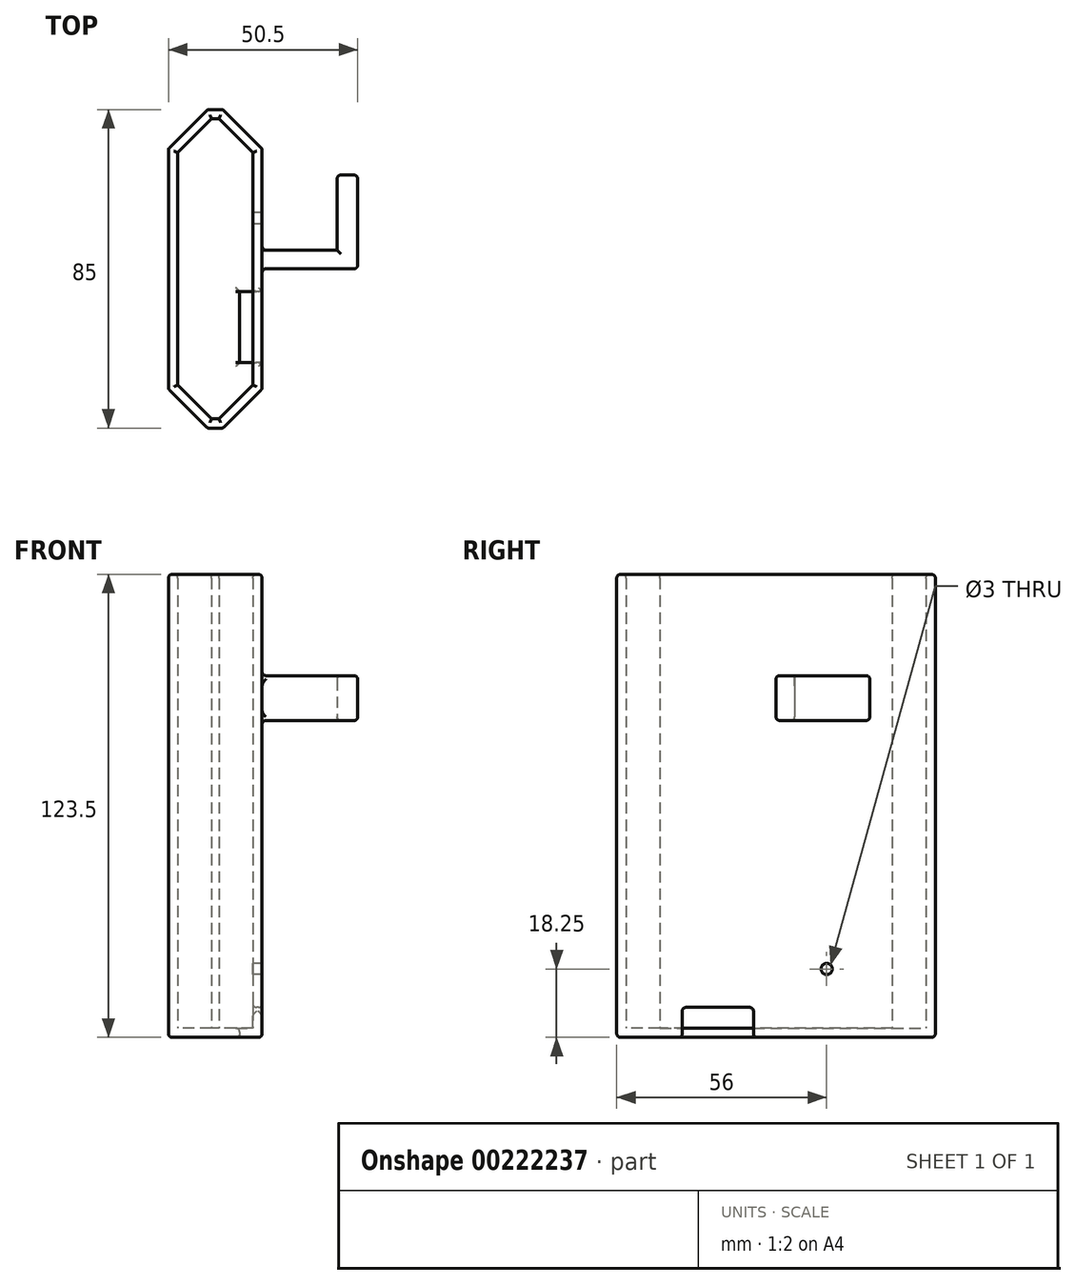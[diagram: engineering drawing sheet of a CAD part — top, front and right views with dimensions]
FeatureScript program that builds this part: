
annotation { "Feature Type Name" : "Feature", "Feature Type Description" : "" }
export const myFeature = defineFeature(function(context is Context, id is Id, definition is map)
    precondition{}
    {
        {
            var Q0;
            Q0=qCreatedBy(makeId("Top.planeOp"),FACE);
            var sketch = newSketch(context, id + "F0", { "sketchPlane" : qUnion([Q0])});
            skPoint(sketch, "E0.middle", {"position": v(0, 0) * mm});
            skPoint(sketch, "E1", {"position": v(-10, 31) * mm});
            skPoint(sketch, "E2", {"position": v(10, 31) * mm});
            skPoint(sketch, "E3", {"position": v(10, -31) * mm});
            skPoint(sketch, "E4", {"position": v(-10, -31) * mm});
            skPoint(sketch, "E5", {"position": v(-1, 40) * mm});
            skPoint(sketch, "E6", {"position": v(-1, -40) * mm});
            skPoint(sketch, "E7", {"position": v(1, 40) * mm});
            skPoint(sketch, "E8", {"position": v(1, -40) * mm});
            skLineSegment(sketch, "E9", {"start": v(1, 40) * mm, "end": v(-1, 40) * mm});
            skLineSegment(sketch, "E10", {"start": v(-1, 40) * mm, "end": v(-10, 31) * mm});
            skLineSegment(sketch, "E11", {"start": v(-10, 31) * mm, "end": v(-10, -31) * mm});
            skLineSegment(sketch, "E12", {"start": v(-10, -31) * mm, "end": v(-1, -40) * mm});
            skLineSegment(sketch, "E13", {"start": v(-1, -40) * mm, "end": v(1, -40) * mm});
            skLineSegment(sketch, "E14", {"start": v(1, -40) * mm, "end": v(10, -31) * mm});
            skLineSegment(sketch, "E15", {"start": v(10, -31) * mm, "end": v(10, 31) * mm});
            skLineSegment(sketch, "E16", {"start": v(10, 31) * mm, "end": v(1, 40) * mm});
            skLineSegment(sketch, "E17.0", {"start": v(12.5, 32.04) * mm, "end": v(2.04, 42.5) * mm});
            skLineSegment(sketch, "E17.1", {"start": v(12.5, -32.04) * mm, "end": v(12.5, 32.04) * mm});
            skLineSegment(sketch, "E17.2", {"start": v(2.04, 42.5) * mm, "end": v(-2.04, 42.5) * mm});
            skLineSegment(sketch, "E17.3", {"start": v(2.04, -42.5) * mm, "end": v(12.5, -32.04) * mm});
            skLineSegment(sketch, "E17.4", {"start": v(-2.04, 42.5) * mm, "end": v(-12.5, 32.04) * mm});
            skLineSegment(sketch, "E17.5", {"start": v(-12.5, 32.04) * mm, "end": v(-12.5, -32.04) * mm});
            skLineSegment(sketch, "E17.6", {"start": v(-12.5, -32.04) * mm, "end": v(-2.04, -42.5) * mm});
            skLineSegment(sketch, "E17.7", {"start": v(-2.04, -42.5) * mm, "end": v(2.04, -42.5) * mm});
            skSolve(sketch);
        }
        {
            var Q0;
            Q0=makeQuery(id+"F0.imprint","IMPRINT",FACE,{"disambiguationData":[TD([[makeQuery(id+"F0.imprint","IMPRINT",EDGE,{"derivedFrom":sQuery(id+"F0.wireOp",EDGE,"E9")}),1.0]])]});
            extrude(context, id + "F1", {"entities" : qUnion([Q0]), "depth" : 2.5 * mm, "offsetDistance" : 25 * mm});
        }
        {
            var Q0;
            Q0=makeQuery(id+"F0.imprint","IMPRINT",FACE,{"disambiguationData":[TD([[makeQuery(id+"F0.imprint","IMPRINT",EDGE,{"derivedFrom":sQuery(id+"F0.wireOp",EDGE,"E9")}),-1.0]])]});
            extrude(context, id + "F2", {"entities" : qUnion([Q0]), "operationType" : NewBodyOperationType.ADD, "depth" : 123.5 * mm, "offsetDistance" : 25 * mm});
        }
        {
            var Q0;
            {var subQ0=sQuery(id+"F0.wireOp",EDGE,"E16");var subQ1=sQuery(id+"F0.wireOp",EDGE,"E15");var subQ2=sQuery(id+"F0.wireOp",EDGE,"E14");var subQ3=sQuery(id+"F0.wireOp",EDGE,"E13");var subQ4=sQuery(id+"F0.wireOp",EDGE,"E12");var subQ5=sQuery(id+"F0.wireOp",EDGE,"E11");var subQ6=sQuery(id+"F0.wireOp",EDGE,"E10");var subQ7=sQuery(id+"F0.wireOp",EDGE,"E9");Q0=makeQuery(id+"F2.boolean.opBoolean","MERGE",FACE,{"derivedFrom":[makeQuery(id+"F1.opExtrude","CAP_FACE",FACE,{"disambiguationData":[OSD([subQ7,subQ6,subQ5,subQ4,subQ3,subQ2,subQ1,subQ0])],"isStart":true}),makeQuery(id+"F2.opExtrude","CAP_FACE",FACE,{"disambiguationData":[OSD([subQ7,subQ6,subQ5,subQ4,subQ3,subQ2,subQ1,subQ0,sQuery(id+"F0.wireOp",EDGE,"E17.0"),sQuery(id+"F0.wireOp",EDGE,"E17.1"),sQuery(id+"F0.wireOp",EDGE,"E17.2"),sQuery(id+"F0.wireOp",EDGE,"E17.3"),sQuery(id+"F0.wireOp",EDGE,"E17.4"),sQuery(id+"F0.wireOp",EDGE,"E17.5"),sQuery(id+"F0.wireOp",EDGE,"E17.6"),sQuery(id+"F0.wireOp",EDGE,"E17.7")])],"isStart":true})]});}
            var sketch = newSketch(context, id + "F3", { "sketchPlane" : qUnion([Q0])});
            skPoint(sketch, "E18", {"position": v(12.5, 25.04) * mm});
            skPoint(sketch, "E19", {"position": v(12.5, 32.04) * mm});
            skLineSegment(sketch, "E20.bottom", {"start": v(12.5, 25.04) * mm, "end": v(6.5, 25.04) * mm});
            skLineSegment(sketch, "E20.top", {"start": v(12.5, 6.04) * mm, "end": v(6.5, 6.04) * mm});
            skLineSegment(sketch, "E20.left", {"start": v(12.5, 25.04) * mm, "end": v(12.5, 6.04) * mm});
            skLineSegment(sketch, "E20.right", {"start": v(6.5, 25.04) * mm, "end": v(6.5, 6.04) * mm});
            skPoint(sketch, "E21", {"position": v(12.5, 0) * mm});
            skPoint(sketch, "E22", {"position": v(-12.5, 0) * mm});
            skSolve(sketch);
        }
        {
            var Q0;
            Q0=makeQuery(id+"F3.imprint","IMPRINT",FACE,{"disambiguationData":[TD([[makeQuery(id+"F3.imprint","IMPRINT",EDGE,{"derivedFrom":sQuery(id+"F3.wireOp",EDGE,"E20.bottom")}),1.0]])]});
            extrude(context, id + "F4", {"entities" : qUnion([Q0]), "operationType" : NewBodyOperationType.REMOVE, "oppositeDirection" : true, "depth" : 8 * mm, "offsetDistance" : 25 * mm});
        }
        {
            var Q0;
            Q0=makeQuery(id+"F2.opExtrude","SWEPT_FACE",FACE,{"disambiguationData":[OSD([sQuery(id+"F0.wireOp",EDGE,"E17.1")])]});
            var sketch = newSketch(context, id + "F5", { "sketchPlane" : qUnion([Q0])});
            skPoint(sketch, "E23", {"position": v(0, 18.25) * mm});
            skPoint(sketch, "E24", {"position": v(13.5, 18.25) * mm});
            skPoint(sketch, "E25", {"position": v(0, 96.5) * mm});
            skPoint(sketch, "E26", {"position": v(0, 84.5) * mm});
            skLineSegment(sketch, "E27.bottom", {"start": v(0, 96.5) * mm, "end": v(5, 96.5) * mm});
            skLineSegment(sketch, "E27.top", {"start": v(0, 84.5) * mm, "end": v(5, 84.5) * mm});
            skLineSegment(sketch, "E27.left", {"start": v(0, 96.5) * mm, "end": v(0, 84.5) * mm});
            skLineSegment(sketch, "E27.right", {"start": v(5, 96.5) * mm, "end": v(5, 84.5) * mm});
            skLineSegment(sketch, "E28.bottom", {"start": v(5, 96.5) * mm, "end": v(25, 96.5) * mm});
            skLineSegment(sketch, "E28.top", {"start": v(5, 84.5) * mm, "end": v(25, 84.5) * mm});
            skLineSegment(sketch, "E28.right", {"start": v(25, 96.5) * mm, "end": v(25, 84.5) * mm});
            skSolve(sketch);
        }
        {
            var Q0;
            Q0=sQuery(id+"F5.wireOp",VERTEX,"E24");
            var Q1;
            Q1=makeQuery(id+"F1.opExtrude","SWEPT_BODY",BODY,{"disambiguationData":[OSD([sQuery(id+"F0.wireOp",EDGE,"E9"),sQuery(id+"F0.wireOp",EDGE,"E10"),sQuery(id+"F0.wireOp",EDGE,"E11"),sQuery(id+"F0.wireOp",EDGE,"E12"),sQuery(id+"F0.wireOp",EDGE,"E13"),sQuery(id+"F0.wireOp",EDGE,"E14"),sQuery(id+"F0.wireOp",EDGE,"E15"),sQuery(id+"F0.wireOp",EDGE,"E16")])]});
            hole(context, id + "F6", {"style" : HoleStyle.SIMPLE, "endStyle" : HoleEndStyle.BLIND, "holeDiameter" : 3 * mm, "majorDiameter" : 5 * mm, "holeDepth" : 5 * mm, "isTappedThrough" : true, "tappedDepth" : 12 * mm, "tapClearance" : 3, "locations" : qUnion([Q0]), "scope" : qUnion([Q1])});
        }
        {
            var Q0;
            Q0=makeQuery(id+"F5.imprint","IMPRINT",FACE,{"disambiguationData":[TD([[makeQuery(id+"F5.imprint","IMPRINT",EDGE,{"derivedFrom":sQuery(id+"F5.wireOp",EDGE,"E27.bottom")}),-1.0]])]});
            extrude(context, id + "F7", {"entities" : qUnion([Q0]), "operationType" : NewBodyOperationType.ADD, "depth" : 25.5 * mm, "offsetDistance" : 25 * mm});
        }
        {
            var Q0;
            Q0=makeQuery(id+"F5.imprint","IMPRINT",FACE,{"disambiguationData":[TD([[makeQuery(id+"F5.imprint","IMPRINT",EDGE,{"derivedFrom":sQuery(id+"F5.wireOp",EDGE,"E28.bottom")}),-1.0]])]});
            extrude(context, id + "F8", {"entities" : qUnion([Q0]), "operationType" : NewBodyOperationType.ADD, "depth" : 25.5 * mm, "offsetDistance" : 25 * mm, "hasSecondDirection" : true, "secondDirectionOppositeDirection" : false, "secondDirectionDepth" : 20 * mm});
        }
        {
            var Q0;
            Q0=makeQuery(id+"F2.opExtrude","CAP_FACE",FACE,{"disambiguationData":[OSD([sQuery(id+"F0.wireOp",EDGE,"E9"),sQuery(id+"F0.wireOp",EDGE,"E10"),sQuery(id+"F0.wireOp",EDGE,"E11"),sQuery(id+"F0.wireOp",EDGE,"E12"),sQuery(id+"F0.wireOp",EDGE,"E13"),sQuery(id+"F0.wireOp",EDGE,"E14"),sQuery(id+"F0.wireOp",EDGE,"E15"),sQuery(id+"F0.wireOp",EDGE,"E16"),sQuery(id+"F0.wireOp",EDGE,"E17.0"),sQuery(id+"F0.wireOp",EDGE,"E17.1"),sQuery(id+"F0.wireOp",EDGE,"E17.2"),sQuery(id+"F0.wireOp",EDGE,"E17.3"),sQuery(id+"F0.wireOp",EDGE,"E17.4"),sQuery(id+"F0.wireOp",EDGE,"E17.5"),sQuery(id+"F0.wireOp",EDGE,"E17.6"),sQuery(id+"F0.wireOp",EDGE,"E17.7")])],"isStart":false});
            var Q1;
            Q1=makeQuery(id+"F8.boolean.opBoolean","MERGE",FACE,{"derivedFrom":[makeQuery(id+"F7.opExtrude","SWEPT_FACE",FACE,{"disambiguationData":[OSD([sQuery(id+"F5.wireOp",EDGE,"E27.bottom")])]}),makeQuery(id+"F8.opExtrude","SWEPT_FACE",FACE,{"disambiguationData":[OSD([sQuery(id+"F5.wireOp",EDGE,"E28.bottom")])]})]});
            var Q2;
            Q2=makeQuery(id+"F8.boolean.opBoolean","MERGE",FACE,{"derivedFrom":[makeQuery(id+"F7.opExtrude","SWEPT_FACE",FACE,{"disambiguationData":[OSD([sQuery(id+"F5.wireOp",EDGE,"E27.top")])]}),makeQuery(id+"F8.opExtrude","SWEPT_FACE",FACE,{"disambiguationData":[OSD([sQuery(id+"F5.wireOp",EDGE,"E28.top")])]})]});
            var Q3;
            {var subQ0=sQuery(id+"F0.wireOp",EDGE,"E16");var subQ1=sQuery(id+"F0.wireOp",EDGE,"E15");var subQ2=sQuery(id+"F0.wireOp",EDGE,"E14");var subQ3=sQuery(id+"F0.wireOp",EDGE,"E13");var subQ4=sQuery(id+"F0.wireOp",EDGE,"E12");var subQ5=sQuery(id+"F0.wireOp",EDGE,"E11");var subQ6=sQuery(id+"F0.wireOp",EDGE,"E10");var subQ7=sQuery(id+"F0.wireOp",EDGE,"E9");Q3=makeQuery(id+"F2.boolean.opBoolean","MERGE",FACE,{"derivedFrom":[makeQuery(id+"F1.opExtrude","CAP_FACE",FACE,{"disambiguationData":[OSD([subQ7,subQ6,subQ5,subQ4,subQ3,subQ2,subQ1,subQ0])],"isStart":true}),makeQuery(id+"F2.opExtrude","CAP_FACE",FACE,{"disambiguationData":[OSD([subQ7,subQ6,subQ5,subQ4,subQ3,subQ2,subQ1,subQ0,sQuery(id+"F0.wireOp",EDGE,"E17.0"),sQuery(id+"F0.wireOp",EDGE,"E17.1"),sQuery(id+"F0.wireOp",EDGE,"E17.2"),sQuery(id+"F0.wireOp",EDGE,"E17.3"),sQuery(id+"F0.wireOp",EDGE,"E17.4"),sQuery(id+"F0.wireOp",EDGE,"E17.5"),sQuery(id+"F0.wireOp",EDGE,"E17.6"),sQuery(id+"F0.wireOp",EDGE,"E17.7")])],"isStart":true})]});}
            var Q4;
            Q4=makeQuery(id+"F2.opExtrude","SWEPT_EDGE",EDGE,{"disambiguationData":[OSD([sQuery(id+"F0.wireOp",EDGE,"E17.2"),sQuery(id+"F0.wireOp",EDGE,"E17.4")])]});
            var Q5;
            Q5=makeQuery(id+"F2.opExtrude","SWEPT_EDGE",EDGE,{"disambiguationData":[OSD([sQuery(id+"F0.wireOp",EDGE,"E17.4"),sQuery(id+"F0.wireOp",EDGE,"E17.5")])]});
            var Q6;
            Q6=makeQuery(id+"F2.opExtrude","SWEPT_EDGE",EDGE,{"disambiguationData":[OSD([sQuery(id+"F0.wireOp",EDGE,"E17.5"),sQuery(id+"F0.wireOp",EDGE,"E17.6")])]});
            var Q7;
            Q7=makeQuery(id+"F2.opExtrude","SWEPT_EDGE",EDGE,{"disambiguationData":[OSD([sQuery(id+"F0.wireOp",EDGE,"E17.6"),sQuery(id+"F0.wireOp",EDGE,"E17.7")])]});
            var Q8;
            Q8=makeQuery(id+"F2.opExtrude","SWEPT_EDGE",EDGE,{"disambiguationData":[OSD([sQuery(id+"F0.wireOp",EDGE,"E17.0"),sQuery(id+"F0.wireOp",EDGE,"E17.2")])]});
            var Q9;
            Q9=makeQuery(id+"F2.opExtrude","SWEPT_EDGE",EDGE,{"disambiguationData":[OSD([sQuery(id+"F0.wireOp",EDGE,"E17.0"),sQuery(id+"F0.wireOp",EDGE,"E17.1")])]});
            var Q10;
            Q10=makeQuery(id+"F2.opExtrude","SWEPT_EDGE",EDGE,{"disambiguationData":[OSD([sQuery(id+"F0.wireOp",EDGE,"E17.1"),sQuery(id+"F0.wireOp",EDGE,"E17.3")])]});
            var Q11;
            Q11=makeQuery(id+"F2.opExtrude","SWEPT_EDGE",EDGE,{"disambiguationData":[OSD([sQuery(id+"F0.wireOp",EDGE,"E17.3"),sQuery(id+"F0.wireOp",EDGE,"E17.7")])]});
            var Q12;
            Q12=makeQuery(id+"F4.boolean.opBoolean","COPY",FACE,{"derivedFrom":makeQuery(id+"F4.opExtrude","CAP_FACE",FACE,{"disambiguationData":[OSD([sQuery(id+"F3.wireOp",EDGE,"E20.bottom"),sQuery(id+"F3.wireOp",EDGE,"E20.top"),sQuery(id+"F3.wireOp",EDGE,"E20.left"),sQuery(id+"F3.wireOp",EDGE,"E20.right")])],"isStart":false})});
            var Q13;
            Q13=makeQuery(id+"F4.boolean.opBoolean","INTERSECT",EDGE,{"derivedFrom":[makeQuery(id+"F1.opExtrude","CAP_FACE",FACE,{"disambiguationData":[OSD([sQuery(id+"F0.wireOp",EDGE,"E9"),sQuery(id+"F0.wireOp",EDGE,"E10"),sQuery(id+"F0.wireOp",EDGE,"E11"),sQuery(id+"F0.wireOp",EDGE,"E12"),sQuery(id+"F0.wireOp",EDGE,"E13"),sQuery(id+"F0.wireOp",EDGE,"E14"),sQuery(id+"F0.wireOp",EDGE,"E15"),sQuery(id+"F0.wireOp",EDGE,"E16")])],"isStart":false}),makeQuery(id+"F4.opExtrude","SWEPT_FACE",FACE,{"disambiguationData":[OSD([sQuery(id+"F3.wireOp",EDGE,"E20.right")])]})]});
            var Q14;
            Q14=makeQuery(id+"F8.opExtrude","SWEPT_FACE",FACE,{"disambiguationData":[OSD([sQuery(id+"F5.wireOp",EDGE,"E28.right")])]});
            var Q15;
            Q15=makeQuery(id+"F7.opExtrude","CAP_EDGE",EDGE,{"disambiguationData":[OSD([sQuery(id+"F5.wireOp",EDGE,"E27.left")])],"isStart":false});
            fillet(context, id + "F9", {"entities" : qUnion([Q0, Q1, Q2, Q3, Q4, Q5, Q6, Q7, Q8, Q9, Q10, Q11, Q12, Q13, Q14, Q15]), "radius" : 1 * mm, "tangentPropagation" : true, "allowEdgeOverflow" : false});
        }
    });
